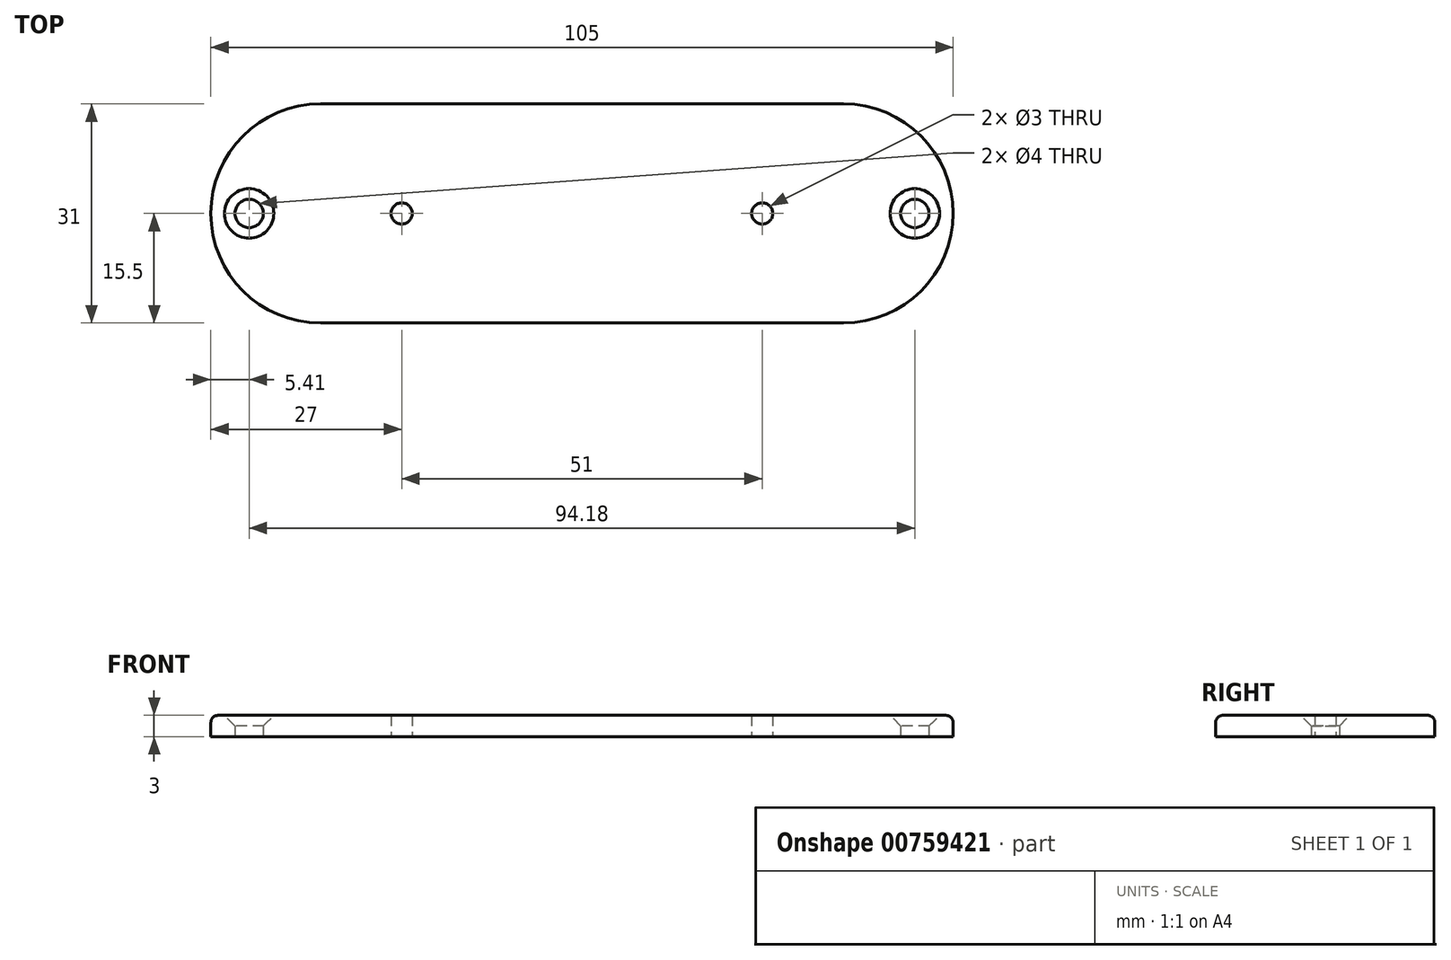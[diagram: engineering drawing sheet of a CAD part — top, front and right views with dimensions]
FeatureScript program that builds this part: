
annotation { "Feature Type Name" : "Feature", "Feature Type Description" : "" }
export const myFeature = defineFeature(function(context is Context, id is Id, definition is map)
    precondition{}
    {
        {
            var Q0;
            Q0=qCreatedBy(makeId("Top.planeOp"),FACE);
            var sketch = newSketch(context, id + "F0", { "sketchPlane" : qUnion([Q0])});
            skLineSegment(sketch, "E0.bottom", {"start": v(37, -15.5) * mm, "end": v(-37, -15.5) * mm});
            skLineSegment(sketch, "E0.top", {"start": v(37, 15.5) * mm, "end": v(-37, 15.5) * mm});
            skPoint(sketch, "E0.middle", {"position": v(0, 0) * mm});
            skArc(sketch, "E1", {"start": v(-37, 15.5) * mm, "mid": v(-52.5, 0) * mm, "end": v(-37, -15.5) * mm});
            skPoint(sketch, "E1.centerSnap0", {"position": v(-52.5, 0) * mm});
            skArc(sketch, "E2.MirrorCS", {"start": v(37, 15.5) * mm, "mid": v(52.5, 0) * mm, "end": v(37, -15.5) * mm});
            skPoint(sketch, "E3.orphan", {"position": v(-52.5, 15.5) * mm});
            skPoint(sketch, "E4.orphan", {"position": v(52.5, 15.5) * mm});
            skPoint(sketch, "E5.orphan", {"position": v(52.5, -15.5) * mm});
            skPoint(sketch, "E6.orphan", {"position": v(-52.5, -15.5) * mm});
            skCircle(sketch, "E7", {"center": v(-25.5, 0) * mm, "radius": 1.5 * mm});
            skCircle(sketch, "E8.MirrorC", {"center": v(25.5, 0) * mm, "radius": 1.5 * mm});
            skCircle(sketch, "E9", {"center": v(-47.1, 0) * mm, "radius": 2 * mm});
            skCircle(sketch, "E10.MirrorC", {"center": v(47.1, 0) * mm, "radius": 2 * mm});
            skSolve(sketch);
        }
        {
            var Q0;
            Q0 = qSketchRegion(id + "F0", true);
            extrude(context, id + "F1", {"entities" : qUnion([Q0]), "depth" : 3 * mm, "offsetDistance" : 25 * mm});
        }
        {
            var Q0;
            Q0=makeQuery(id+"F1.opExtrude","CAP_EDGE",EDGE,{"disambiguationData":[OSD([sQuery(id+"F0.wireOp",EDGE,"E9")])],"isStart":false});
            chamfer(context, id + "F2", {"entities" : qUnion([Q0]), "width" : 1.5 * mm, "tangentPropagation" : true});
        }
        {
            var Q0;
            Q0=makeQuery(id+"F1.opExtrude","CAP_EDGE",EDGE,{"disambiguationData":[OSD([sQuery(id+"F0.wireOp",EDGE,"E10.MirrorC")])],"isStart":false});
            chamfer(context, id + "F3", {"entities" : qUnion([Q0]), "width" : 1.5 * mm, "tangentPropagation" : true});
        }
        {
            var Q0;
            Q0=makeQuery(id+"F1.opExtrude","CAP_EDGE",EDGE,{"disambiguationData":[OSD([sQuery(id+"F0.wireOp",EDGE,"E0.bottom")])],"isStart":false});
            var Q1;
            Q1=makeQuery(id+"F1.opExtrude","CAP_EDGE",EDGE,{"disambiguationData":[OSD([sQuery(id+"F0.wireOp",EDGE,"E1")])],"isStart":false});
            var Q2;
            Q2=makeQuery(id+"F1.opExtrude","CAP_EDGE",EDGE,{"disambiguationData":[OSD([sQuery(id+"F0.wireOp",EDGE,"E0.top")])],"isStart":false});
            var Q3;
            Q3=makeQuery(id+"F1.opExtrude","CAP_EDGE",EDGE,{"disambiguationData":[OSD([sQuery(id+"F0.wireOp",EDGE,"E2.MirrorCS")])],"isStart":false});
            fillet(context, id + "F4", {"entities" : qUnion([Q0, Q1, Q2, Q3]), "radius" : 1 * mm, "tangentPropagation" : true, "allowEdgeOverflow" : false});
        }
    });
